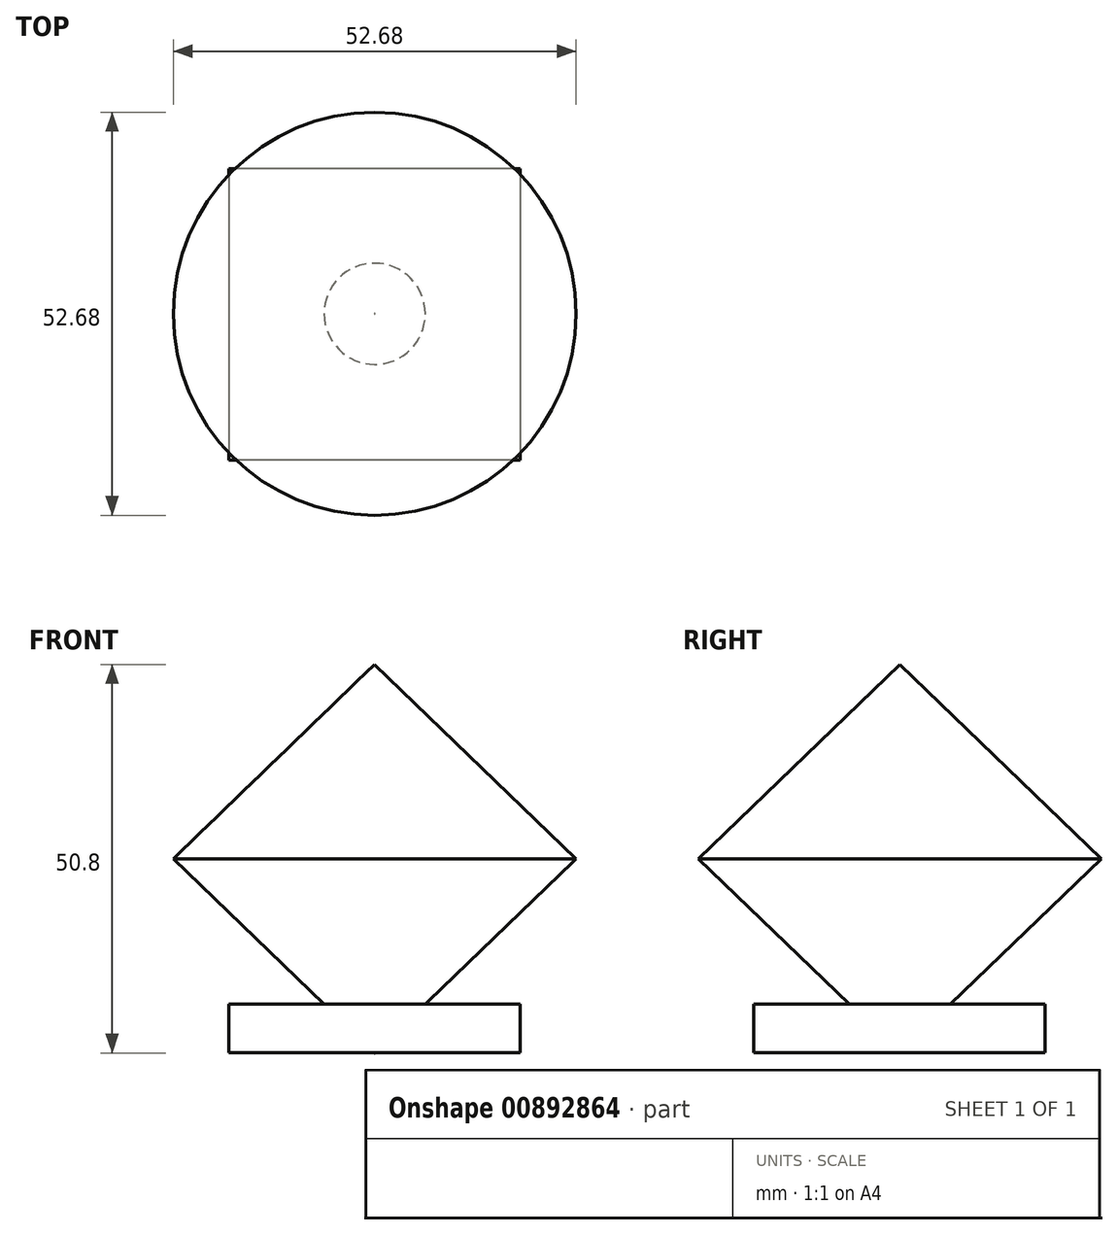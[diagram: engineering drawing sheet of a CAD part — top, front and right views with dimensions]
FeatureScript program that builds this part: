
annotation { "Feature Type Name" : "Feature", "Feature Type Description" : "" }
export const myFeature = defineFeature(function(context is Context, id is Id, definition is map)
    precondition{}
    {
        {
            var Q0;
            Q0=qCreatedBy(makeId("Front.planeOp"),FACE);
            var sketch = newSketch(context, id + "F0", { "sketchPlane" : qUnion([Q0])});
            skLineSegment(sketch, "E0.MirrorCS", {"start": v(0, 25.4) * mm, "end": v(26.34, 0) * mm});
            skLineSegment(sketch, "E1.MirrorCS", {"start": v(0, -25.4) * mm, "end": v(26.34, 0) * mm});
            skLineSegment(sketch, "E2", {"start": v(0, 25.4) * mm, "end": v(0, -25.4) * mm});
            skSolve(sketch);
        }
        {
            var Q0;
            Q0 = qSketchRegion(id + "F0", true);
            var Q1;
            Q1=sQuery(id+"F0.wireOp",EDGE,"E2");
            revolve(context, id + "F1", {"surfaceOperationType" : NewSurfaceOperationType.NEW, "entities" : qUnion([Q0]), "axis" : qUnion([Q1]), "revolveType" : RevolveType.FULL});
        }
        {
            var Q0;
            Q0=qCreatedBy(makeId("Right.planeOp"),FACE);
            var sketch = newSketch(context, id + "F2", { "sketchPlane" : qUnion([Q0])});
            skLineSegment(sketch, "E3", {"start": v(-0.1, -25.38) * mm, "end": v(-19.14, -25.38) * mm});
            skLineSegment(sketch, "E4", {"start": v(-19.14, -25.38) * mm, "end": v(-19.14, -19.03) * mm});
            skLineSegment(sketch, "E5", {"start": v(-19.14, -19.03) * mm, "end": v(-0.1, -19.03) * mm});
            skLineSegment(sketch, "E6.MirrorCS", {"start": v(18.96, -19.03) * mm, "end": v(-0.1, -19.03) * mm});
            skLineSegment(sketch, "E7.MirrorCS", {"start": v(18.96, -25.38) * mm, "end": v(18.96, -19.03) * mm});
            skLineSegment(sketch, "E8.MirrorCS", {"start": v(-0.1, -25.38) * mm, "end": v(18.96, -25.38) * mm});
            skSolve(sketch);
        }
        {
            var Q0;
            Q0=makeQuery(id+"F2.imprint","IMPRINT",FACE,{"disambiguationData":[TD([[makeQuery(id+"F2.imprint","IMPRINT",EDGE,{"derivedFrom":sQuery(id+"F2.wireOp",EDGE,"E3")}),-1.0]])]});
            extrude(context, id + "F3", {"entities" : qUnion([Q0]), "operationType" : NewBodyOperationType.ADD, "depth" : 19.05 * mm, "offsetDistance" : 25.4 * mm, "hasSecondDirection" : true, "secondDirectionOppositeDirection" : true, "secondDirectionDepth" : 19.05 * mm});
        }
    });
